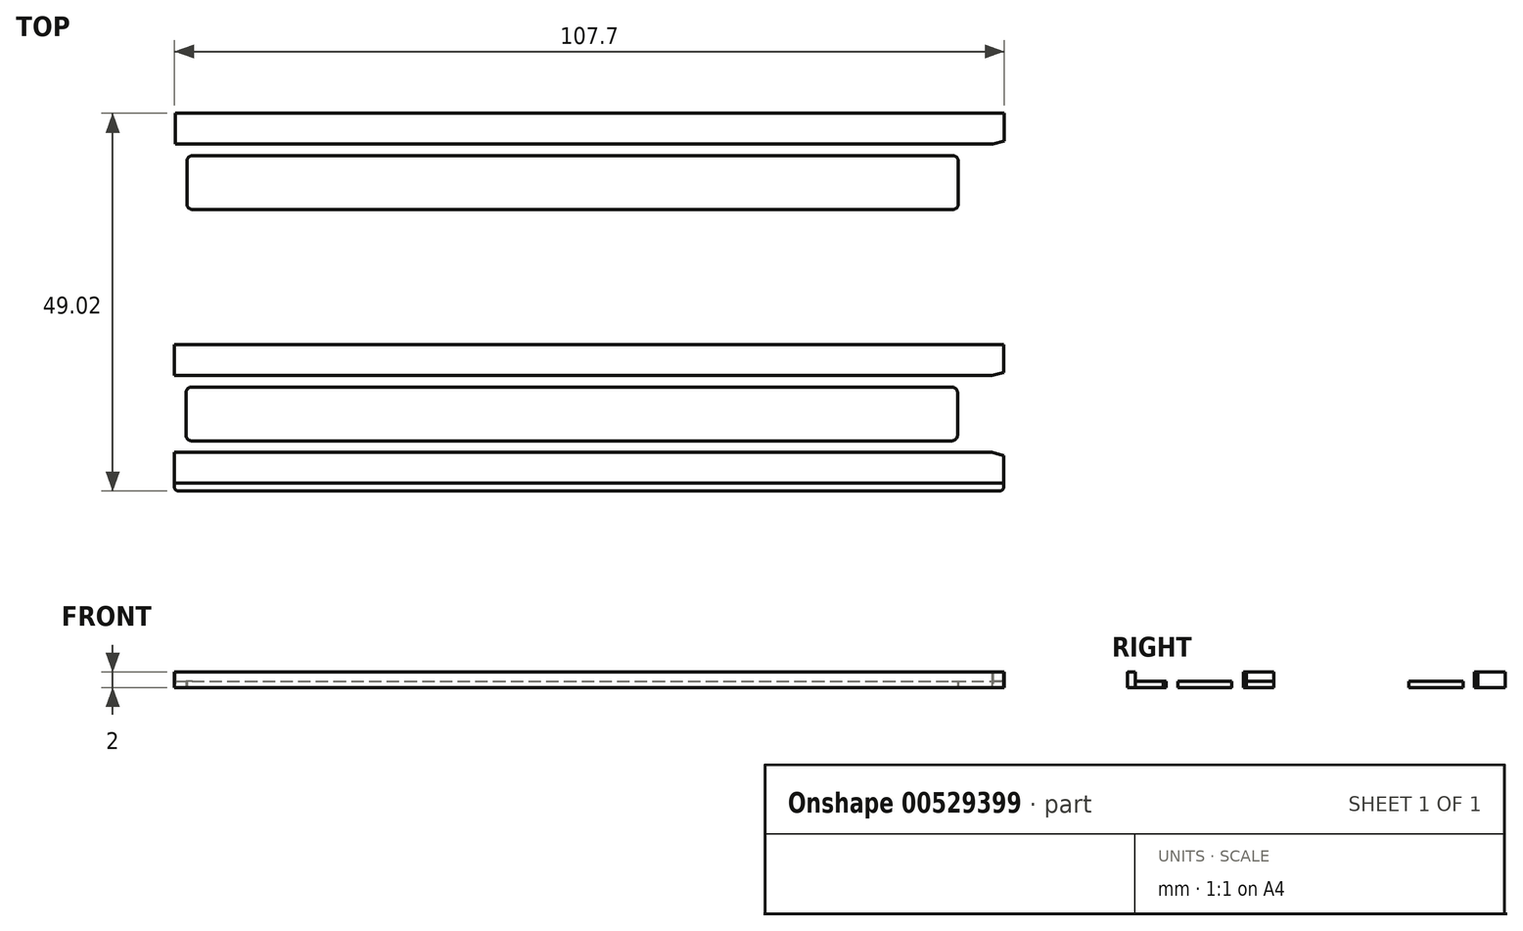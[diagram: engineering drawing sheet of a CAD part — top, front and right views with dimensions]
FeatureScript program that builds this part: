
annotation { "Feature Type Name" : "Feature", "Feature Type Description" : "" }
export const myFeature = defineFeature(function(context is Context, id is Id, definition is map)
    precondition{}
    {
        {
            var Q0;
            Q0=qCreatedBy(makeId("Top.planeOp"),FACE);
            var sketch = newSketch(context, id + "F0", { "sketchPlane" : qUnion([Q0])});
            skLineSegment(sketch, "E0.bottom", {"start": v(-57.67, 1) * mm, "end": v(48.93, 1) * mm});
            skLineSegment(sketch, "E0.top", {"start": v(-57.67, -19) * mm, "end": v(48.93, -19) * mm});
            skLineSegment(sketch, "E0.left", {"start": v(-58.17, 0.5) * mm, "end": v(-58.17, -6.4) * mm});
            skLineSegment(sketch, "E0.right", {"start": v(49.43, 0.5) * mm, "end": v(49.43, -3.6) * mm});
            skLineSegment(sketch, "E1.bottom", {"start": v(-58.17, 0) * mm, "end": v(49.43, 0) * mm});
            skLineSegment(sketch, "E1.left", {"start": v(-58.17, 0) * mm, "end": v(-58.17, 0.5) * mm});
            skLineSegment(sketch, "E1.right", {"start": v(49.43, 0) * mm, "end": v(49.43, 0.5) * mm});
            skLineSegment(sketch, "E2.top", {"start": v(-58.17, -18) * mm, "end": v(49.43, -18) * mm});
            skLineSegment(sketch, "E2.left", {"start": v(-58.17, -18.5) * mm, "end": v(-58.17, -18) * mm});
            skLineSegment(sketch, "E2.right", {"start": v(49.43, -18.5) * mm, "end": v(49.43, -18) * mm});
            skLineSegment(sketch, "E3.top", {"start": v(-58.17, -4) * mm, "end": v(49.18, -4) * mm});
            skLineSegment(sketch, "E3.left", {"start": v(-58.17, 0) * mm, "end": v(-58.17, -4) * mm});
            skLineSegment(sketch, "E3.right", {"start": v(49.43, 0) * mm, "end": v(49.43, -3.6) * mm});
            skLineSegment(sketch, "E4.top", {"start": v(-58.17, -14) * mm, "end": v(49.18, -14) * mm});
            skLineSegment(sketch, "E4.left", {"start": v(-58.17, -18) * mm, "end": v(-58.17, -14) * mm});
            skLineSegment(sketch, "E4.right", {"start": v(49.43, -18) * mm, "end": v(49.43, -14.4) * mm});
            skLineSegment(sketch, "E5", {"start": v(-61.58, -9) * mm, "end": v(-62.45, -8.5) * mm});
            skLineSegment(sketch, "E6", {"start": v(-62.45, -8.5) * mm, "end": v(-62.45, -6.23) * mm});
            skLineSegment(sketch, "E7", {"start": v(-62.17, -5.98) * mm, "end": v(-58.17, -6.4) * mm});
            skLineSegment(sketch, "E8.MirrorCS", {"start": v(-62.17, -12.02) * mm, "end": v(-58.17, -11.6) * mm});
            skLineSegment(sketch, "E9.MirrorCS", {"start": v(-62.45, -9.5) * mm, "end": v(-62.45, -11.77) * mm});
            skLineSegment(sketch, "E10.MirrorCS", {"start": v(-61.58, -9) * mm, "end": v(-62.45, -9.5) * mm});
            skLineSegment(sketch, "E11", {"start": v(44.95, -5.85) * mm, "end": v(49.16, -6.27) * mm});
            skLineSegment(sketch, "E12.MirrorCS", {"start": v(44.95, -12.15) * mm, "end": v(49.16, -11.73) * mm});
            skLineSegment(sketch, "E13", {"start": v(44.95, -5.85) * mm, "end": v(44.95, -12.15) * mm});
            skLineSegment(sketch, "E14.trimOffspring", {"start": v(49.43, -14.4) * mm, "end": v(49.43, -18.5) * mm});
            skLineSegment(sketch, "E15", {"start": v(49.43, -4.25) * mm, "end": v(49.43, -6.02) * mm});
            skLineSegment(sketch, "E16", {"start": v(49.43, -11.98) * mm, "end": v(49.43, -13.75) * mm});
            skLineSegment(sketch, "E17.trimOffspring", {"start": v(-58.17, -11.6) * mm, "end": v(-58.17, -18.5) * mm});
            skLineSegment(sketch, "E18", {"start": v(49.43, -3.6) * mm, "end": v(47.93, -4) * mm});
            skLineSegment(sketch, "E19", {"start": v(49.43, -14.4) * mm, "end": v(47.93, -14) * mm});
            skLineSegment(sketch, "E20.bottom", {"start": v(-55.92, -5.5) * mm, "end": v(42.7, -5.5) * mm});
            skLineSegment(sketch, "E20.top", {"start": v(-55.92, -12.5) * mm, "end": v(42.7, -12.5) * mm});
            skLineSegment(sketch, "E20.left", {"start": v(-56.67, -6.25) * mm, "end": v(-56.67, -11.75) * mm});
            skLineSegment(sketch, "E20.right", {"start": v(43.45, -6.25) * mm, "end": v(43.45, -11.75) * mm});
            skLineSegment(sketch, "E21.bottom", {"start": v(-57.57, 31.02) * mm, "end": v(49.03, 31.02) * mm});
            skLineSegment(sketch, "E21.top", {"start": v(-57.57, 11.02) * mm, "end": v(49.03, 11.02) * mm});
            skLineSegment(sketch, "E21.left", {"start": v(-58.07, 30.52) * mm, "end": v(-58.07, 23.62) * mm});
            skLineSegment(sketch, "E21.right", {"start": v(49.53, 30.52) * mm, "end": v(49.53, 26.42) * mm});
            skLineSegment(sketch, "E22.bottom", {"start": v(-58.07, 30.02) * mm, "end": v(49.53, 30.02) * mm});
            skLineSegment(sketch, "E22.left", {"start": v(-58.07, 30.02) * mm, "end": v(-58.07, 30.52) * mm});
            skLineSegment(sketch, "E22.right", {"start": v(49.53, 30.02) * mm, "end": v(49.53, 30.52) * mm});
            skLineSegment(sketch, "E23.top", {"start": v(-58.07, 12.02) * mm, "end": v(49.53, 12.02) * mm});
            skLineSegment(sketch, "E23.left", {"start": v(-58.07, 11.52) * mm, "end": v(-58.07, 12.02) * mm});
            skLineSegment(sketch, "E23.right", {"start": v(49.53, 11.52) * mm, "end": v(49.53, 12.02) * mm});
            skLineSegment(sketch, "E24.top", {"start": v(-58.07, 26.02) * mm, "end": v(49.28, 26.02) * mm});
            skLineSegment(sketch, "E24.left", {"start": v(-58.07, 30.02) * mm, "end": v(-58.07, 26.02) * mm});
            skLineSegment(sketch, "E24.right", {"start": v(49.53, 30.02) * mm, "end": v(49.53, 26.42) * mm});
            skLineSegment(sketch, "E25.top", {"start": v(-58.07, 16.02) * mm, "end": v(49.28, 16.02) * mm});
            skLineSegment(sketch, "E25.left", {"start": v(-58.07, 12.02) * mm, "end": v(-58.07, 16.02) * mm});
            skLineSegment(sketch, "E25.right", {"start": v(49.53, 12.02) * mm, "end": v(49.53, 15.62) * mm});
            skLineSegment(sketch, "E26", {"start": v(-61.48, 21.02) * mm, "end": v(-62.34, 21.52) * mm});
            skLineSegment(sketch, "E27", {"start": v(-62.34, 21.52) * mm, "end": v(-62.34, 23.79) * mm});
            skLineSegment(sketch, "E28", {"start": v(-62.07, 24.04) * mm, "end": v(-58.07, 23.62) * mm});
            skLineSegment(sketch, "E29.MirrorCS", {"start": v(-62.07, 18) * mm, "end": v(-58.07, 18.42) * mm});
            skLineSegment(sketch, "E30.MirrorCS", {"start": v(-62.34, 20.52) * mm, "end": v(-62.34, 18.24) * mm});
            skLineSegment(sketch, "E31.MirrorCS", {"start": v(-61.48, 21.02) * mm, "end": v(-62.34, 20.52) * mm});
            skLineSegment(sketch, "E32", {"start": v(45.06, 24.17) * mm, "end": v(49.26, 23.74) * mm});
            skLineSegment(sketch, "E33.MirrorCS", {"start": v(45.06, 17.87) * mm, "end": v(49.26, 18.29) * mm});
            skLineSegment(sketch, "E34", {"start": v(45.06, 24.17) * mm, "end": v(45.06, 17.87) * mm});
            skLineSegment(sketch, "E35.trimOffspring", {"start": v(49.53, 15.62) * mm, "end": v(49.53, 11.52) * mm});
            skLineSegment(sketch, "E36", {"start": v(49.53, 25.77) * mm, "end": v(49.53, 24) * mm});
            skLineSegment(sketch, "E37", {"start": v(49.53, 18.04) * mm, "end": v(49.53, 16.27) * mm});
            skLineSegment(sketch, "E38.trimOffspring", {"start": v(-58.07, 18.42) * mm, "end": v(-58.07, 11.52) * mm});
            skLineSegment(sketch, "E39", {"start": v(49.53, 26.42) * mm, "end": v(48.03, 26.02) * mm});
            skLineSegment(sketch, "E40", {"start": v(49.53, 15.62) * mm, "end": v(48.03, 16.02) * mm});
            skLineSegment(sketch, "E41.bottom", {"start": v(-55.82, 24.52) * mm, "end": v(42.8, 24.52) * mm});
            skLineSegment(sketch, "E41.top", {"start": v(-55.82, 17.52) * mm, "end": v(42.8, 17.52) * mm});
            skLineSegment(sketch, "E41.left", {"start": v(-56.57, 23.77) * mm, "end": v(-56.57, 18.27) * mm});
            skLineSegment(sketch, "E41.right", {"start": v(43.56, 23.77) * mm, "end": v(43.56, 18.27) * mm});
            skPoint(sketch, "E42.visualSharp", {"position": v(-56.57, 24.52) * mm});
            skArc(sketch, "E42.filletArc", {"start": v(-55.82, 24.52) * mm, "mid": v(-56.35, 24.3) * mm, "end": v(-56.57, 23.77) * mm});
            skPoint(sketch, "E43.visualSharp", {"position": v(-56.57, 17.52) * mm});
            skArc(sketch, "E43.filletArc", {"start": v(-56.57, 18.27) * mm, "mid": v(-56.35, 17.74) * mm, "end": v(-55.82, 17.52) * mm});
            skPoint(sketch, "E44.visualSharp", {"position": v(43.56, 24.52) * mm});
            skArc(sketch, "E44.filletArc", {"start": v(43.56, 23.77) * mm, "mid": v(43.34, 24.3) * mm, "end": v(42.8, 24.52) * mm});
            skPoint(sketch, "E45.visualSharp", {"position": v(43.56, 17.52) * mm});
            skArc(sketch, "E45.filletArc", {"start": v(42.8, 17.52) * mm, "mid": v(43.34, 17.74) * mm, "end": v(43.56, 18.27) * mm});
            skPoint(sketch, "E46.visualSharp", {"position": v(49.53, 23.72) * mm});
            skArc(sketch, "E46.filletArc", {"start": v(49.26, 23.74) * mm, "mid": v(49.45, 23.8) * mm, "end": v(49.53, 24) * mm});
            skPoint(sketch, "E47.visualSharp", {"position": v(49.53, 18.32) * mm});
            skArc(sketch, "E47.filletArc", {"start": v(49.53, 18.04) * mm, "mid": v(49.45, 18.23) * mm, "end": v(49.26, 18.29) * mm});
            skPoint(sketch, "E48.visualSharp", {"position": v(-62.34, 24.07) * mm});
            skArc(sketch, "E48.filletArc", {"start": v(-62.07, 24.04) * mm, "mid": v(-62.26, 23.97) * mm, "end": v(-62.34, 23.79) * mm});
            skPoint(sketch, "E49.visualSharp", {"position": v(-62.34, 17.97) * mm});
            skArc(sketch, "E49.filletArc", {"start": v(-62.34, 18.24) * mm, "mid": v(-62.26, 18.06) * mm, "end": v(-62.07, 18) * mm});
            skPoint(sketch, "E50.visualSharp", {"position": v(49.43, -6.3) * mm});
            skArc(sketch, "E50.filletArc", {"start": v(49.16, -6.27) * mm, "mid": v(49.35, -6.2) * mm, "end": v(49.43, -6.02) * mm});
            skPoint(sketch, "E51.visualSharp", {"position": v(49.43, -11.7) * mm});
            skArc(sketch, "E51.filletArc", {"start": v(49.43, -11.98) * mm, "mid": v(49.35, -11.8) * mm, "end": v(49.16, -11.73) * mm});
            skPoint(sketch, "E52.visualSharp", {"position": v(-62.45, -5.95) * mm});
            skArc(sketch, "E52.filletArc", {"start": v(-62.17, -5.98) * mm, "mid": v(-62.36, -6.04) * mm, "end": v(-62.45, -6.23) * mm});
            skPoint(sketch, "E53.visualSharp", {"position": v(-62.45, -12.05) * mm});
            skArc(sketch, "E53.filletArc", {"start": v(-62.45, -11.77) * mm, "mid": v(-62.36, -11.96) * mm, "end": v(-62.17, -12.02) * mm});
            skPoint(sketch, "E54.visualSharp", {"position": v(-56.67, -5.5) * mm});
            skArc(sketch, "E54.filletArc", {"start": v(-55.92, -5.5) * mm, "mid": v(-56.45, -5.72) * mm, "end": v(-56.67, -6.25) * mm});
            skPoint(sketch, "E55.visualSharp", {"position": v(-56.67, -12.5) * mm});
            skArc(sketch, "E55.filletArc", {"start": v(-56.67, -11.75) * mm, "mid": v(-56.45, -12.28) * mm, "end": v(-55.92, -12.5) * mm});
            skPoint(sketch, "E56.visualSharp", {"position": v(43.45, -5.5) * mm});
            skArc(sketch, "E56.filletArc", {"start": v(43.45, -6.25) * mm, "mid": v(43.23, -5.72) * mm, "end": v(42.7, -5.5) * mm});
            skPoint(sketch, "E57.visualSharp", {"position": v(43.45, -12.5) * mm});
            skArc(sketch, "E57.filletArc", {"start": v(42.7, -12.5) * mm, "mid": v(43.23, -12.28) * mm, "end": v(43.45, -11.75) * mm});
            skPoint(sketch, "E58.visualSharp", {"position": v(49.43, 1) * mm});
            skArc(sketch, "E58.filletArc", {"start": v(49.43, 0.5) * mm, "mid": v(49.28, 0.85) * mm, "end": v(48.93, 1) * mm});
            skPoint(sketch, "E59.visualSharp", {"position": v(49.43, -19) * mm});
            skArc(sketch, "E59.filletArc", {"start": v(48.93, -19) * mm, "mid": v(49.28, -18.85) * mm, "end": v(49.43, -18.5) * mm});
            skPoint(sketch, "E60.visualSharp", {"position": v(-58.17, 1) * mm});
            skArc(sketch, "E60.filletArc", {"start": v(-57.67, 1) * mm, "mid": v(-58.02, 0.85) * mm, "end": v(-58.17, 0.5) * mm});
            skPoint(sketch, "E61.visualSharp", {"position": v(-58.17, -19) * mm});
            skArc(sketch, "E61.filletArc", {"start": v(-58.17, -18.5) * mm, "mid": v(-58.02, -18.85) * mm, "end": v(-57.67, -19) * mm});
            skPoint(sketch, "E62.visualSharp", {"position": v(-58.07, 11.02) * mm});
            skArc(sketch, "E62.filletArc", {"start": v(-58.07, 11.52) * mm, "mid": v(-57.92, 11.16) * mm, "end": v(-57.57, 11.02) * mm});
            skPoint(sketch, "E63.visualSharp", {"position": v(-58.07, 31.02) * mm});
            skArc(sketch, "E63.filletArc", {"start": v(-57.57, 31.02) * mm, "mid": v(-57.92, 30.87) * mm, "end": v(-58.07, 30.52) * mm});
            skPoint(sketch, "E64.visualSharp", {"position": v(49.53, 31.02) * mm});
            skArc(sketch, "E64.filletArc", {"start": v(49.53, 30.52) * mm, "mid": v(49.39, 30.87) * mm, "end": v(49.03, 31.02) * mm});
            skPoint(sketch, "E65.visualSharp", {"position": v(49.53, 11.02) * mm});
            skArc(sketch, "E65.filletArc", {"start": v(49.03, 11.02) * mm, "mid": v(49.39, 11.16) * mm, "end": v(49.53, 11.52) * mm});
            skPoint(sketch, "E66.visualSharp", {"position": v(49.53, 16.02) * mm});
            skArc(sketch, "E66.filletArc", {"start": v(49.28, 16.02) * mm, "mid": v(49.46, 16.1) * mm, "end": v(49.53, 16.27) * mm});
            skPoint(sketch, "E67.visualSharp", {"position": v(49.53, 26.02) * mm});
            skArc(sketch, "E67.filletArc", {"start": v(49.53, 25.77) * mm, "mid": v(49.46, 25.94) * mm, "end": v(49.28, 26.02) * mm});
            skPoint(sketch, "E68.visualSharp", {"position": v(49.43, -4) * mm});
            skArc(sketch, "E68.filletArc", {"start": v(49.43, -4.25) * mm, "mid": v(49.36, -4.07) * mm, "end": v(49.18, -4) * mm});
            skPoint(sketch, "E69.visualSharp", {"position": v(49.43, -14) * mm});
            skArc(sketch, "E69.filletArc", {"start": v(49.18, -14) * mm, "mid": v(49.36, -13.93) * mm, "end": v(49.43, -13.75) * mm});
            skSolve(sketch);
        }
        {
            var Q0;
            Q0=makeQuery(id+"F0.imprint","IMPRINT",FACE,{"disambiguationData":[TD([[makeQuery(id+"F0.imprint","IMPRINT",EDGE,{"derivedFrom":sQuery(id+"F0.wireOp",EDGE,"E0.bottom")}),-1.0]])]});
            var Q1;
            {var subQ3=sQuery(id+"F0.wireOp",EDGE,"E0.left");Q1=makeQuery(id+"F0.imprint","IMPRINT",FACE,{"disambiguationData":[TD([[makeQuery(id+"F0.imprint","IMPRINT",EDGE,{"derivedFrom":subQ3}),1.0]])]});}
            var Q2;
            {var subQ0=sQuery(id+"F0.wireOp",EDGE,"E0.top");Q2=makeQuery(id+"F0.imprint","IMPRINT",FACE,{"disambiguationData":[TD([[makeQuery(id+"F0.imprint","IMPRINT",EDGE,{"derivedFrom":subQ0}),1.0]])]});}
            var Q3;
            Q3=makeQuery(id+"F0.imprint","IMPRINT",FACE,{"disambiguationData":[TD([[makeQuery(id+"F0.imprint","IMPRINT",EDGE,{"derivedFrom":sQuery(id+"F0.wireOp",EDGE,"E21.bottom")}),-1.0]])]});
            var Q4;
            {var subQ5=sQuery(id+"F0.wireOp",EDGE,"E21.left");Q4=makeQuery(id+"F0.imprint","IMPRINT",FACE,{"disambiguationData":[TD([[makeQuery(id+"F0.imprint","IMPRINT",EDGE,{"derivedFrom":subQ5}),1.0]])]});}
            var Q5;
            {var subQ0=sQuery(id+"F0.wireOp",EDGE,"E21.top");Q5=makeQuery(id+"F0.imprint","IMPRINT",FACE,{"disambiguationData":[TD([[makeQuery(id+"F0.imprint","IMPRINT",EDGE,{"derivedFrom":subQ0}),1.0]])]});}
            extrude(context, id + "F1", {"entities" : qUnion([Q0, Q1, Q2, Q3, Q4, Q5]), "depth" : 2 * mm, "offsetDistance" : 25 * mm});
        }
        {
            var Q0;
            Q0=makeQuery(id+"F0.imprint","IMPRINT",FACE,{"disambiguationData":[TD([[makeQuery(id+"F0.imprint","IMPRINT",EDGE,{"derivedFrom":sQuery(id+"F0.wireOp",EDGE,"E1.bottom")}),-1.0]])]});
            var Q1;
            Q1=makeQuery(id+"F0.imprint","IMPRINT",FACE,{"disambiguationData":[TD([[makeQuery(id+"F0.imprint","IMPRINT",EDGE,{"derivedFrom":sQuery(id+"F0.wireOp",EDGE,"E20.bottom")}),-1.0]])]});
            var Q2;
            {var subQ1=sQuery(id+"F0.wireOp",EDGE,"E2.top");Q2=makeQuery(id+"F0.imprint","IMPRINT",FACE,{"disambiguationData":[TD([[makeQuery(id+"F0.imprint","IMPRINT",EDGE,{"derivedFrom":subQ1}),1.0]])]});}
            var Q3;
            Q3=makeQuery(id+"F0.imprint","IMPRINT",FACE,{"disambiguationData":[TD([[makeQuery(id+"F0.imprint","IMPRINT",EDGE,{"derivedFrom":sQuery(id+"F0.wireOp",EDGE,"E22.bottom")}),-1.0]])]});
            var Q4;
            Q4=makeQuery(id+"F0.imprint","IMPRINT",FACE,{"disambiguationData":[TD([[makeQuery(id+"F0.imprint","IMPRINT",EDGE,{"derivedFrom":sQuery(id+"F0.wireOp",EDGE,"E41.bottom")}),-1.0]])]});
            var Q5;
            {var subQ1=sQuery(id+"F0.wireOp",EDGE,"E23.top");Q5=makeQuery(id+"F0.imprint","IMPRINT",FACE,{"disambiguationData":[TD([[makeQuery(id+"F0.imprint","IMPRINT",EDGE,{"derivedFrom":subQ1}),1.0]])]});}
            extrude(context, id + "F2", {"entities" : qUnion([Q0, Q1, Q2, Q3, Q4, Q5]), "depth" : 0.8 * mm, "offsetDistance" : 25 * mm});
        }
    });
